FCSTD DOCUMENT  (FreeCAD 0.14R3702 (Git))
Label: 2020TBracket
License: CC-BY 3.0
LicenseURL: http://creativecommons.org/licenses/by/3.0/
objects: Sketcher::SketchObject×1
note: 1 computed .brp shape members not serialized (recipe doc carries the construction recipe); baked Part::Feature solids carry a one-line shape summary decoded from their .brp

FEATURE [Sketcher::SketchObject] Sketch
  sketch-geometry (12):
    g0: LineSegment StartX=0 StartY=0 StartZ=0 EndX=60 EndY=0 EndZ=0
    g1: LineSegment StartX=60 StartY=0 StartZ=0 EndX=60 EndY=20 EndZ=0
    g2: LineSegment StartX=0 StartY=0 StartZ=0 EndX=0 EndY=20 EndZ=0
    g3: LineSegment StartX=0 StartY=20 StartZ=0 EndX=20 EndY=20 EndZ=0
    g4: LineSegment StartX=20 StartY=20 StartZ=0 EndX=20 EndY=40 EndZ=0
    g5: LineSegment StartX=60 StartY=20 StartZ=0 EndX=40 EndY=20 EndZ=0
    g6: LineSegment StartX=40 StartY=20 StartZ=0 EndX=40 EndY=40 EndZ=0
    g7: LineSegment StartX=20 StartY=40 StartZ=0 EndX=40 EndY=40 EndZ=0
    g8: Circle CenterX=10 CenterY=10 CenterZ=0 NormalX=0 NormalY=0 NormalZ=1 Radius=2.01
    g9: Circle CenterX=30 CenterY=10 CenterZ=0 NormalX=0 NormalY=0 NormalZ=1 Radius=2.01
    g10: Circle CenterX=50 CenterY=10 CenterZ=0 NormalX=0 NormalY=0 NormalZ=1 Radius=2.01
    g11: Circle CenterX=30 CenterY=30 CenterZ=0 NormalX=0 NormalY=0 NormalZ=1 Radius=2.01
  constraints (30):
    c: Coincident(g0,g-1)
    c: Horizontal(g0)
    c: Coincident(g1,g0)
    c: Vertical(g1)
    c: DistanceY(g1) = 20
    c: Coincident(g2,g-1)
    c: PointOnObject(g2,g-2)
    c: Vertical(g2)
    c: PointOnObject(g3,g2)
    c: Horizontal(g3)
    c: Coincident(g4,g3)
    c: Vertical(g4)
    c: Coincident(g5,g1)
    c: Horizontal(g5)
    c: Equal(g1,g5)
    c: Equal(g3,g5)
    c: Equal(g4,g3)
    c: Coincident(g6,g5)
    c: Vertical(g6)
    c: Equal(g4,g6)
    c: Coincident(g7,g4)
    c: Coincident(g7,g6)
    c: Horizontal(g7)
    c: Radius(g9) = 2.01
    c: Equal(g9,g10)
    c: Equal(g9,g11)
    c: Equal(g9,g8)
    c: Equal(g7,g4)
    c: Equal(g6,g7)
    c: DistanceX(g0) = 60
